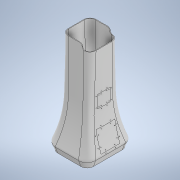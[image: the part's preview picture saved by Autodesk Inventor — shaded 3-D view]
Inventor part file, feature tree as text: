
AUTODESK INVENTOR PART (.ipt)
format: ipt  version: 2021 (Build 250183000, 183)  size: 3,223,040 bytes
history: native  units: mm
features: sketch x36, other x29, plane x13, hole x11, extrude x10, projected_geometry x9, chamfer x3, pattern_linear x3, fillet x2, mirror x2, loft x1, shell x1
ambient origin geometry x8: Origin, YZ Plane, XZ Plane, XY Plane, X Axis, Y Axis, Z Axis, Center Point
bodies: Body1 (feature_tree), Body2 (feature_tree), Body3 (feature_tree), Body4 (feature_tree), Body5 (feature_tree), Body6 (feature_tree)
feature tree (120):
  other  "實體1"
  extrude  "擠出1"  Depth=284.5mm
  plane  "工作平面1"
  sketch  "草圖2"
  plane  "工作平面8"
  sketch  "草圖10"
  plane  "工作平面9"
  sketch  "草圖12"
  plane  "工作平面10"
  sketch  "草圖13"
  plane  "工作平面11"
  sketch  "草圖14"
  plane  "工作平面12"
  sketch  "草圖15"
  plane  "工作平面13"
  sketch  "草圖16"
  plane  "工作平面14"
  sketch  "草圖17"
  plane  "工作平面15"
  loft  "斷面混成1"
  shell  "薄殼1"  Thickness=50.0mm
  hole  "孔1"  [1 undecoded]
  plane  "工作平面16"
  other  "分割1"
  hole  "孔2"  [1 undecoded]
  hole  "孔3"  [1 undecoded]
  extrude  "擠出3"  Depth=225.0mm
  fillet  "圓角1"  Radius=50.0mm
  extrude  "擠出4"  Depth=400.0mm
  hole  "孔6"  [1 undecoded]
  extrude  "擠出6"  Depth=10.0mm
  fillet  "圓角2"  Radius=25.0mm
  plane  "工作平面17"
  extrude  "擠出7"  Depth=400.0mm
  hole  "孔7"  [1 undecoded]
  extrude  "擠出8"  Depth=10.0mm
  mirror  "鏡射3"
  extrude  "擠出9"  Depth=25.0mm
  chamfer  "倒角1"  Distance=400.0mm
  extrude  "擠出10"  Depth=10.0mm
  chamfer  "倒角2"  Distance=25.0mm
  extrude  "擠出11"  Depth=800.0mm
  chamfer  "倒角3"  Distance=400.0mm
  hole  "孔8"  [1 undecoded]
  pattern_linear  "矩形陣列1"  Spacing1=25.0mm  [1 undecoded]
  hole  "孔9"  [1 undecoded]
  pattern_linear  "矩形陣列2"  Count1=40  [1 undecoded]
  hole  "孔10"  [1 undecoded]
  pattern_linear  "矩形陣列3"  Spacing1=25.0mm  [1 undecoded]
  other  "分割2"
  hole  "孔11"  [1 undecoded]
  hole  "孔12"  [1 undecoded]
  plane  "工作平面18"
  mirror  "鏡射4"
  plane  "工作平面19"
  extrude  "擠出12"  Depth=10.0mm
  hole  "孔14"  [1 undecoded]
  sketch  "草圖1"
  sketch  "草圖18"
  sketch  "草圖19"
  sketch  "草圖20"
  other  "Srf2"
  sketch  "草圖21"
  projected_geometry  "投影迴路3"
  sketch  "草圖22"
  projected_geometry  "投影迴路4"
  sketch  "草圖24"
  projected_geometry  "投影迴路10"
  sketch  "草圖25"
  projected_geometry  "投影迴路11"
  sketch  "草圖29"
  projected_geometry  "投影迴路14"
  sketch  "草圖30"
  sketch  "草圖31"
  sketch  "草圖32"
  sketch  "草圖33"
  sketch  "草圖34"
  sketch  "草圖35"
  sketch  "草圖36"
  other  "Srf3"
  sketch  "草圖37"
  sketch  "草圖38"
  sketch  "草圖39"
  sketch  "草圖40"
  projected_geometry  "投影迴路15"
  sketch  "草圖41"
  sketch  "草圖42"
  projected_geometry  "投影迴路16"
  sketch  "草圖43"
  other  "Srf4"
  sketch  "草圖44"
  projected_geometry  "投影迴路17"
  sketch  "草圖45"
  projected_geometry  "投影迴路18"
  sketch  "草圖46"
  sketch  "草圖47"
  sketch  "草圖53"
  other  "擠出表面2"
  other  "擠出表面3"
  other  "擠出表面4"
  other  "投影切割邊5"
  other  "投影切割邊7"
  other  "投影切割邊8"
  other  "投影切割邊9"
  other  "投影切割邊10"
  other  "投影切割邊11"
  other  "投影切割邊12"
  other  "投影切割邊13"
  other  "實體2"
  other  "實體3"
  other  "投影切割邊14"
  other  "投影切割邊15"
  other  "投影切割邊16"
  other  "投影切割邊17"
  other  "投影切割邊18"
  other  "投影切割邊19"
  other  "實體4"
  other  "實體5"
  other  "投影切割邊20"
  other  "投影切割邊21"
note: 14 required parameter values undecoded (feature->parameter linkage not recoverable at this tier; creation-order binding heuristic only, values carry confidence <= 0.55)
